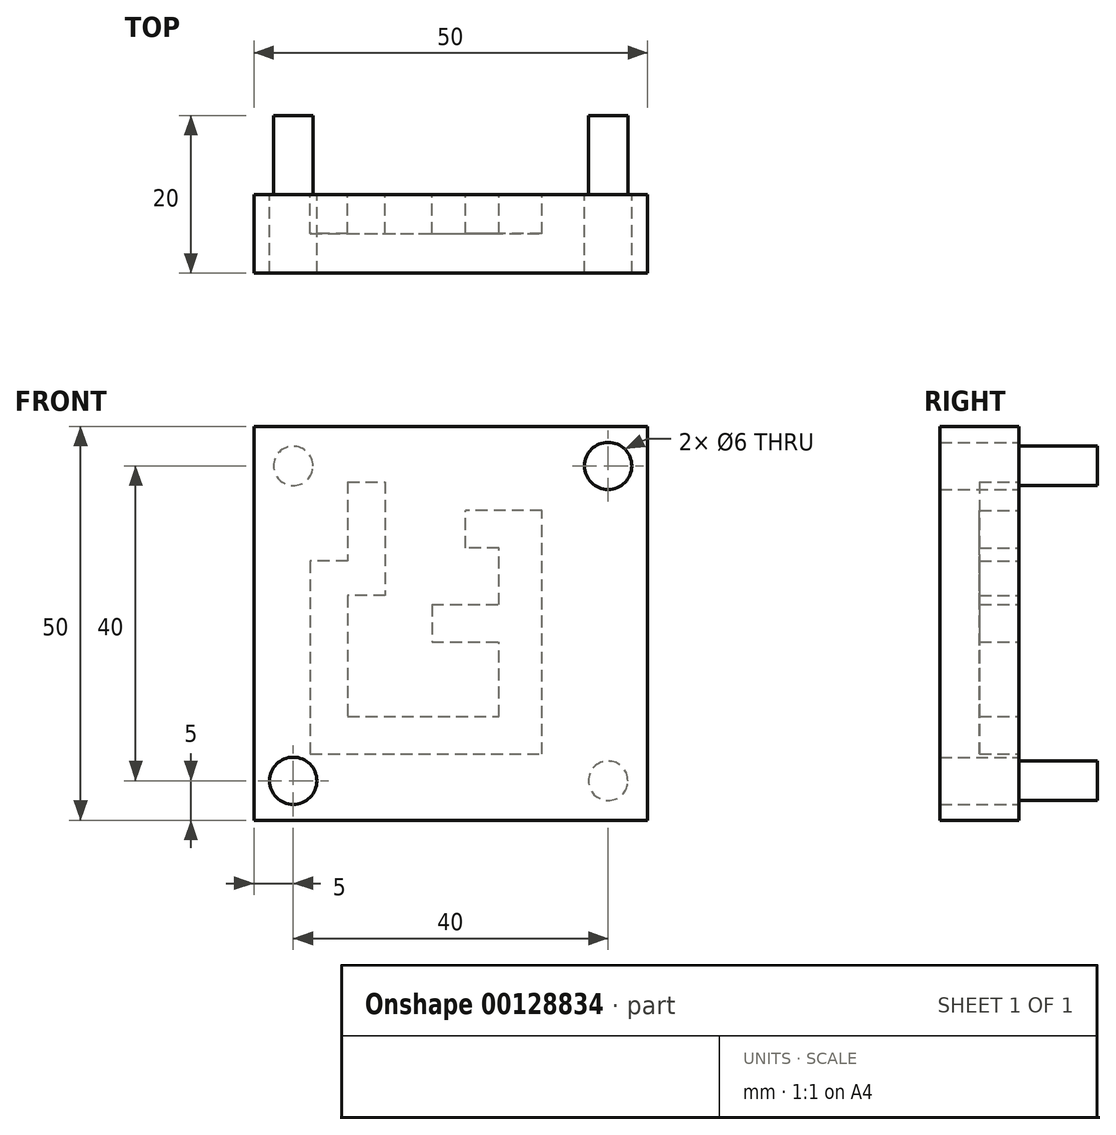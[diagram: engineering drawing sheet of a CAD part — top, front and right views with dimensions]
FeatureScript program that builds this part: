
annotation { "Feature Type Name" : "Feature", "Feature Type Description" : "" }
export const myFeature = defineFeature(function(context is Context, id is Id, definition is map)
    precondition{}
    {
        {
            var Q0;
            Q0=qCreatedBy(makeId("Front.planeOp"),FACE);
            var sketch = newSketch(context, id + "F0", { "sketchPlane" : qUnion([Q0])});
            skLineSegment(sketch, "E0.bottom", {"start": v(25, -25) * mm, "end": v(-25, -25) * mm});
            skLineSegment(sketch, "E0.top", {"start": v(25, 25) * mm, "end": v(-25, 25) * mm});
            skLineSegment(sketch, "E0.left", {"start": v(25, -25) * mm, "end": v(25, 25) * mm});
            skLineSegment(sketch, "E0.right", {"start": v(-25, -25) * mm, "end": v(-25, 25) * mm});
            skPoint(sketch, "E0.middle", {"position": v(0, 0) * mm});
            skLineSegment(sketch, "E1", {"start": v(-25, 25) * mm, "end": v(-13.1, 25) * mm});
            skLineSegment(sketch, "E2", {"start": v(-13.1, 25) * mm, "end": v(-13.1, 17.98) * mm});
            skLineSegment(sketch, "E3", {"start": v(-13.1, 17.98) * mm, "end": v(-8.33, 17.98) * mm});
            skLineSegment(sketch, "E4", {"start": v(-8.33, 17.98) * mm, "end": v(-8.33, 13.22) * mm});
            skLineSegment(sketch, "E5", {"start": v(-13.1, 13.22) * mm, "end": v(-13.1, 17.98) * mm});
            skLineSegment(sketch, "E6", {"start": v(-13.1, 13.22) * mm, "end": v(-13.1, 7.9) * mm});
            skLineSegment(sketch, "E7", {"start": v(-8.33, 13.22) * mm, "end": v(-8.33, 3.54) * mm});
            skLineSegment(sketch, "E8", {"start": v(-13.1, 7.9) * mm, "end": v(-17.86, 7.9) * mm});
            skLineSegment(sketch, "E9", {"start": v(-8.33, 3.54) * mm, "end": v(-13.1, 3.54) * mm});
            skLineSegment(sketch, "E10", {"start": v(-17.86, 7.9) * mm, "end": v(-17.86, 3.54) * mm});
            skLineSegment(sketch, "E11", {"start": v(-17.86, 7.9) * mm, "end": v(-17.86, -16.6) * mm});
            skLineSegment(sketch, "E12", {"start": v(-17.86, -16.6) * mm, "end": v(11.57, -16.6) * mm});
            skLineSegment(sketch, "E13", {"start": v(-13.1, 3.54) * mm, "end": v(-13.1, -11.84) * mm});
            skLineSegment(sketch, "E14", {"start": v(-13.1, -11.84) * mm, "end": v(-4.44, -11.84) * mm});
            skLineSegment(sketch, "E15", {"start": v(11.57, -16.6) * mm, "end": v(11.57, -2.39) * mm});
            skLineSegment(sketch, "E16", {"start": v(-4.44, -11.84) * mm, "end": v(6.13, -11.84) * mm});
            skLineSegment(sketch, "E17.bottom", {"start": v(2.39, 2.39) * mm, "end": v(-2.39, 2.39) * mm});
            skLineSegment(sketch, "E17.top", {"start": v(2.39, -2.39) * mm, "end": v(-2.39, -2.39) * mm});
            skLineSegment(sketch, "E17.right", {"start": v(-2.39, 2.39) * mm, "end": v(-2.39, -2.39) * mm});
            skLineSegment(sketch, "E18", {"start": v(2.39, -2.39) * mm, "end": v(6.13, -2.39) * mm});
            skLineSegment(sketch, "E19", {"start": v(6.13, -11.84) * mm, "end": v(6.13, -2.39) * mm});
            skLineSegment(sketch, "E20", {"start": v(2.39, 2.39) * mm, "end": v(6.13, 2.39) * mm});
            skLineSegment(sketch, "E21", {"start": v(11.57, -2.39) * mm, "end": v(11.57, 2.39) * mm});
            skLineSegment(sketch, "E22", {"start": v(6.13, 2.39) * mm, "end": v(6.13, 9.57) * mm});
            skLineSegment(sketch, "E23", {"start": v(11.57, 2.39) * mm, "end": v(11.57, 9.26) * mm});
            skLineSegment(sketch, "E24", {"start": v(6.13, 9.57) * mm, "end": v(1.86, 9.57) * mm});
            skLineSegment(sketch, "E25", {"start": v(1.86, 9.57) * mm, "end": v(1.86, 14.35) * mm});
            skLineSegment(sketch, "E26", {"start": v(11.57, 9.26) * mm, "end": v(11.57, 14.35) * mm});
            skLineSegment(sketch, "E27", {"start": v(1.86, 14.35) * mm, "end": v(8.93, 14.35) * mm});
            skLineSegment(sketch, "E28", {"start": v(11.57, 13.83) * mm, "end": v(11.57, 14.35) * mm});
            skLineSegment(sketch, "E29", {"start": v(-8.33, 13.22) * mm, "end": v(-13.1, 13.22) * mm});
            skLineSegment(sketch, "E30", {"start": v(2.39, 2.39) * mm, "end": v(2.39, -2.39) * mm});
            skLineSegment(sketch, "E31", {"start": v(11.57, 14.35) * mm, "end": v(8.93, 14.35) * mm});
            skLineSegment(sketch, "E32", {"start": v(-8.33, 17.98) * mm, "end": v(-13.1, 17.98) * mm});
            skLineSegment(sketch, "E33", {"start": v(-13.1, 13.22) * mm, "end": v(-8.33, 13.22) * mm});
            skLineSegment(sketch, "E34", {"start": v(-13.1, 17.98) * mm, "end": v(-13.1, 13.22) * mm});
            skCircle(sketch, "E35", {"center": v(20, 20) * mm, "radius": 3 * mm});
            skCircle(sketch, "E36", {"center": v(-20, -20) * mm, "radius": 3 * mm});
            skCircle(sketch, "E37", {"center": v(-20, 20) * mm, "radius": 2.5 * mm});
            skCircle(sketch, "E38", {"center": v(20, -20) * mm, "radius": 2.5 * mm});
            skSolve(sketch);
        }
        {
            var Q0;
            Q0 = qSketchRegion(id + "F0", true);
            extrude(context, id + "F1", {"entities" : qUnion([Q0]), "endBound" : BoundingType.SYMMETRIC, "depth" : 10 * mm});
        }
        {
            var Q0;
            Q0=makeQuery(id+"F0.imprint","IMPRINT",FACE,{"disambiguationData":[TD([[makeQuery(id+"F0.imprint","IMPRINT",EDGE,{"derivedFrom":sQuery(id+"F0.wireOp",EDGE,"E6")}),1.0]])]});
            var Q1;
            Q1=makeQuery(id+"F0.imprint","IMPRINT",FACE,{"disambiguationData":[TD([[makeQuery(id+"F0.imprint","IMPRINT",EDGE,{"derivedFrom":sQuery(id+"F0.wireOp",EDGE,"E3")}),-1.0]])]});
            var Q2;
            Q2=makeQuery(id+"F0.imprint","IMPRINT",FACE,{"disambiguationData":[TD([[makeQuery(id+"F0.imprint","IMPRINT",EDGE,{"derivedFrom":sQuery(id+"F0.wireOp",EDGE,"E17.bottom")}),1.0]])]});
            extrude(context, id + "F2", {"entities" : qUnion([Q0, Q1, Q2]), "operationType" : NewBodyOperationType.ADD, "depth" : 5 * mm});
        }
        {
            var Q0;
            Q0=makeQuery(id+"F0.imprint","IMPRINT",FACE,{"disambiguationData":[TD([[makeQuery(id+"F0.imprint","IMPRINT",EDGE,{"derivedFrom":sQuery(id+"F0.wireOp",EDGE,"E37")}),1.0]])]});
            var Q1;
            Q1=makeQuery(id+"F0.imprint","IMPRINT",FACE,{"disambiguationData":[TD([[makeQuery(id+"F0.imprint","IMPRINT",EDGE,{"derivedFrom":sQuery(id+"F0.wireOp",EDGE,"E38")}),1.0]])]});
            extrude(context, id + "F3", {"entities" : qUnion([Q0, Q1]), "operationType" : NewBodyOperationType.ADD, "oppositeDirection" : true, "depth" : 15 * mm, "hasSecondDirection" : true, "secondDirectionOppositeDirection" : false, "secondDirectionDepth" : 5 * mm});
        }
    });
